# Revit family: НЕВАТОМ_Вентилятор VKRF-Е (3,15-10)_240619
name_source: partatom
category: Оборудование
units: mm (PartAtom-declared; Revit-internal decimal feet)

## family parameters
Всегда вертикально = Да
На основе рабочей плоскости = Нет
Общий = Нет
При загрузке вырезать с полостями = Нет
Размер круглого соединителя = Использовать диаметр
Тип детали = Нормальный
Точка расчета площади = Нет

## types (11) — shared parameters
ADSK_Единица измерения = шт.
ADSK_Завод-изготовитель = НЕВАТОМ
ADSK_Количество = 1
ADSK_Коэффициент мощности = 1
ADSK_Материал наименование = Оцинкованная сталь
ADSK_Наименование = Вентилятор крышный радиальный с выбросом вверх
ADSK_Напряжение = 380 В
ADSK_Полная мощность = 0 В·А
ADSK_Потеря давления воздуха = 0.0 Па
ADSK_Расход воздуха = 0 м³/ч
Nevatom_URL = https://t.me
h = 20 мм
h9 = 295 мм
Ключевая пометка = Вентиляция
Материал = Сталь ASTM A441

## per-type parameters (varying)
- VKRF № 3,15: ADSK_Марка=VKRF-Е-3,15; ADSK_Масса=46; ADSK_Размер_Высота=665 мм; ADSK_Размер_Длина=520 мм; ADSK_Размер_Ширина=520 мм; ADSK_Ток=14 А; ADSK_Частота вращения вентилятора=750; B=440 мм; D=315 мм; H=665 мм; H1=599 мм; H2=138 мм; H3=569 мм; H4=275 мм; H5=333 мм; L=520 мм; L1=1000 мм; h1=20 мм; l=420 мм; l1=210 мм; l2=210 мм; l3=357 мм; r=69 мм; Высота отвода=130 мм; Мощность двигателя N, кВт=6 кВт; Н6=532 мм; Ширина отвода=270 мм
- VKRF № 4: ADSK_Марка=VKRF-Е-4,0; ADSK_Масса=84.5; ADSK_Размер_Высота=820 мм; ADSK_Размер_Длина=625 мм; ADSK_Размер_Ширина=625 мм; ADSK_Ток=11 А; ADSK_Частота вращения вентилятора=3000; B=530 мм; D=400 мм; H=820 мм; H1=738 мм; H2=170 мм; H3=701 мм; H4=339 мм; H5=410 мм; L=625 мм; L1=1170 мм; h1=25 мм; l=525 мм; l1=263 мм; l2=263 мм; l3=446 мм; r=85 мм; Высота отвода=165 мм; Мощность двигателя N, кВт=6 кВт; Н6=656 мм; Ширина отвода=370 мм
- VKRF № 8: ADSK_Марка=VKRF-Е-8,0; ADSK_Масса=324.3; ADSK_Размер_Высота=1635 мм; ADSK_Размер_Длина=1080 мм; ADSK_Размер_Ширина=1080 мм; ADSK_Ток=8 А; ADSK_Частота вращения вентилятора=750; B=1005 мм; D=800 мм; H=1635 мм; H1=1472 мм; H2=338 мм; H3=1398 мм; H4=677 мм; H5=818 мм; L=1080 мм; L1=1950 мм; h1=49 мм; l=980 мм; l1=490 мм; l2=490 мм; l3=833 мм; r=169 мм; Высота отвода=340 мм; Мощность двигателя N, кВт=3 кВт; Н6=1308 мм; Ширина отвода=740 мм
- VKRF № 7,1: ADSK_Марка=VKRF-Е-7,1; ADSK_Масса=269.5; ADSK_Размер_Высота=1310 мм; ADSK_Размер_Длина=920 мм; ADSK_Размер_Ширина=920 мм; ADSK_Ток=6 А; ADSK_Частота вращения вентилятора=750; B=840 мм; D=710 мм; H=1310 мм; H1=1179 мм; H2=271 мм; H3=1120 мм; H4=542 мм; H5=655 мм; L=920 мм; L1=1750 мм; h1=39 мм; l=820 мм; l1=410 мм; l2=410 мм; l3=697 мм; r=136 мм; Высота отвода=300 мм; Мощность двигателя N, кВт=2 кВт; Н6=1048 мм; Ширина отвода=680 мм
- VKRF № 3,55: ADSK_Марка=VKRF-Е-3,55; ADSK_Масса=62.1; ADSK_Размер_Высота=755 мм; ADSK_Размер_Длина=555 мм; ADSK_Размер_Ширина=555 мм; ADSK_Ток=6 А; ADSK_Частота вращения вентилятора=3000; B=480 мм; D=355 мм; H=755 мм; H1=680 мм; H2=156 мм; H3=646 мм; H4=313 мм; H5=378 мм; L=555 мм; L1=1085 мм; h1=23 мм; l=455 мм; l1=228 мм; l2=228 мм; l3=387 мм; r=78 мм; Высота отвода=150 мм; Мощность двигателя N, кВт=3000 кВт; Н6=604 мм; Ширина отвода=315 мм
- VKRF № 4,5: ADSK_Марка=VKRF-Е-4,5; ADSK_Масса=141.4; ADSK_Размер_Высота=1010 мм; ADSK_Размер_Длина=655 мм; ADSK_Размер_Ширина=655 мм; ADSK_Ток=21 А; ADSK_Частота вращения вентилятора=3000; B=580 мм; D=450 мм; H=1010 мм; H1=909 мм; H2=209 мм; H3=864 мм; H4=418 мм; H5=505 мм; L=655 мм; L1=1275 мм; h1=30 мм; l=555 мм; l1=278 мм; l2=278 мм; l3=472 мм; r=105 мм; Высота отвода=190 мм; Мощность двигателя N, кВт=11 кВт; Н6=808 мм; Ширина отвода=425 мм
- VKRF № 5: ADSK_Марка=VKRF-Е-5,0; ADSK_Масса=143; ADSK_Размер_Высота=855 мм; ADSK_Размер_Длина=710 мм; ADSK_Размер_Ширина=710 мм; ADSK_Ток=21 А; ADSK_Частота вращения вентилятора=3000; B=630 мм; D=500 мм; H=855 мм; H1=770 мм; H2=177 мм; H3=731 мм; H4=354 мм; H5=428 мм; L=710 мм; L1=1360 мм; h1=26 мм; l=610 мм; l1=305 мм; l2=305 мм; l3=519 мм; r=88 мм; Высота отвода=205 мм; Мощность двигателя N, кВт=11 кВт; Н6=684 мм; Ширина отвода=480 мм
- VKRF № 5,6: ADSK_Марка=VKRF-Е-5,6; ADSK_Масса=132.6; ADSK_Размер_Высота=930 мм; ADSK_Размер_Длина=765 мм; ADSK_Размер_Ширина=765 мм; ADSK_Ток=9 А; ADSK_Частота вращения вентилятора=1500; B=690 мм; D=560 мм; H=930 мм; H1=837 мм; H2=193 мм; H3=795 мм; H4=385 мм; H5=465 мм; L=765 мм; L1=1470 мм; h1=28 мм; l=665 мм; l1=333 мм; l2=333 мм; l3=565 мм; r=96 мм; Высота отвода=240 мм; Мощность двигателя N, кВт=4 кВт; Н6=744 мм; Ширина отвода=520 мм
- VKRF № 6,3: ADSK_Марка=VKRF-Е-6,3; ADSK_Масса=147; ADSK_Размер_Высота=1150 мм; ADSK_Размер_Длина=850 мм; ADSK_Размер_Ширина=850 мм; ADSK_Ток=9 А; ADSK_Частота вращения вентилятора=1500; B=755 мм; D=630 мм; H=1150 мм; H1=1035 мм; H2=238 мм; H3=983 мм; H4=476 мм; H5=575 мм; L=850 мм; L1=1595 мм; h1=35 мм; l=750 мм; l1=375 мм; l2=375 мм; l3=638 мм; r=119 мм; Высота отвода=265 мм; Мощность двигателя N, кВт=4 кВт; Н6=920 мм; Ширина отвода=595 мм
- VKRF № 10: ADSK_Марка=VKRF-Е-10,0; ADSK_Масса=597.5; ADSK_Размер_Высота=1830 мм; ADSK_Размер_Длина=1315 мм; ADSK_Размер_Ширина=1315 мм; ADSK_Ток=14 А; ADSK_Частота вращения вентилятора=750; B=1180 мм; D=1000 мм; H=1830 мм; H1=1647 мм; H2=379 мм; H3=1565 мм; H4=758 мм; H5=915 мм; L=1315 мм; L1=2320 мм; h1=55 мм; l=1215 мм; l1=608 мм; l2=608 мм; l3=1033 мм; r=189 мм; Высота отвода=406 мм; Мощность двигателя N, кВт=6 кВт; Н6=1464 мм; Ширина отвода=948 мм
- VKRF № 9: ADSK_Марка=VKRF-Е-9,0; ADSK_Масса=459; ADSK_Размер_Высота=1710 мм; ADSK_Размер_Длина=1080 мм; ADSK_Размер_Ширина=1080 мм; ADSK_Ток=8 А; ADSK_Частота вращения вентилятора=750; B=1005 мм; D=900 мм; H=1710 мм; H1=1539 мм; H2=354 мм; H3=1462 мм; H4=708 мм; H5=855 мм; L=1080 мм; L1=2135 мм; h1=51 мм; l=980 мм; l1=490 мм; l2=490 мм; l3=833 мм; r=177 мм; Высота отвода=380 мм; Мощность двигателя N, кВт=3 кВт; Н6=1368 мм; Ширина отвода=845 мм
